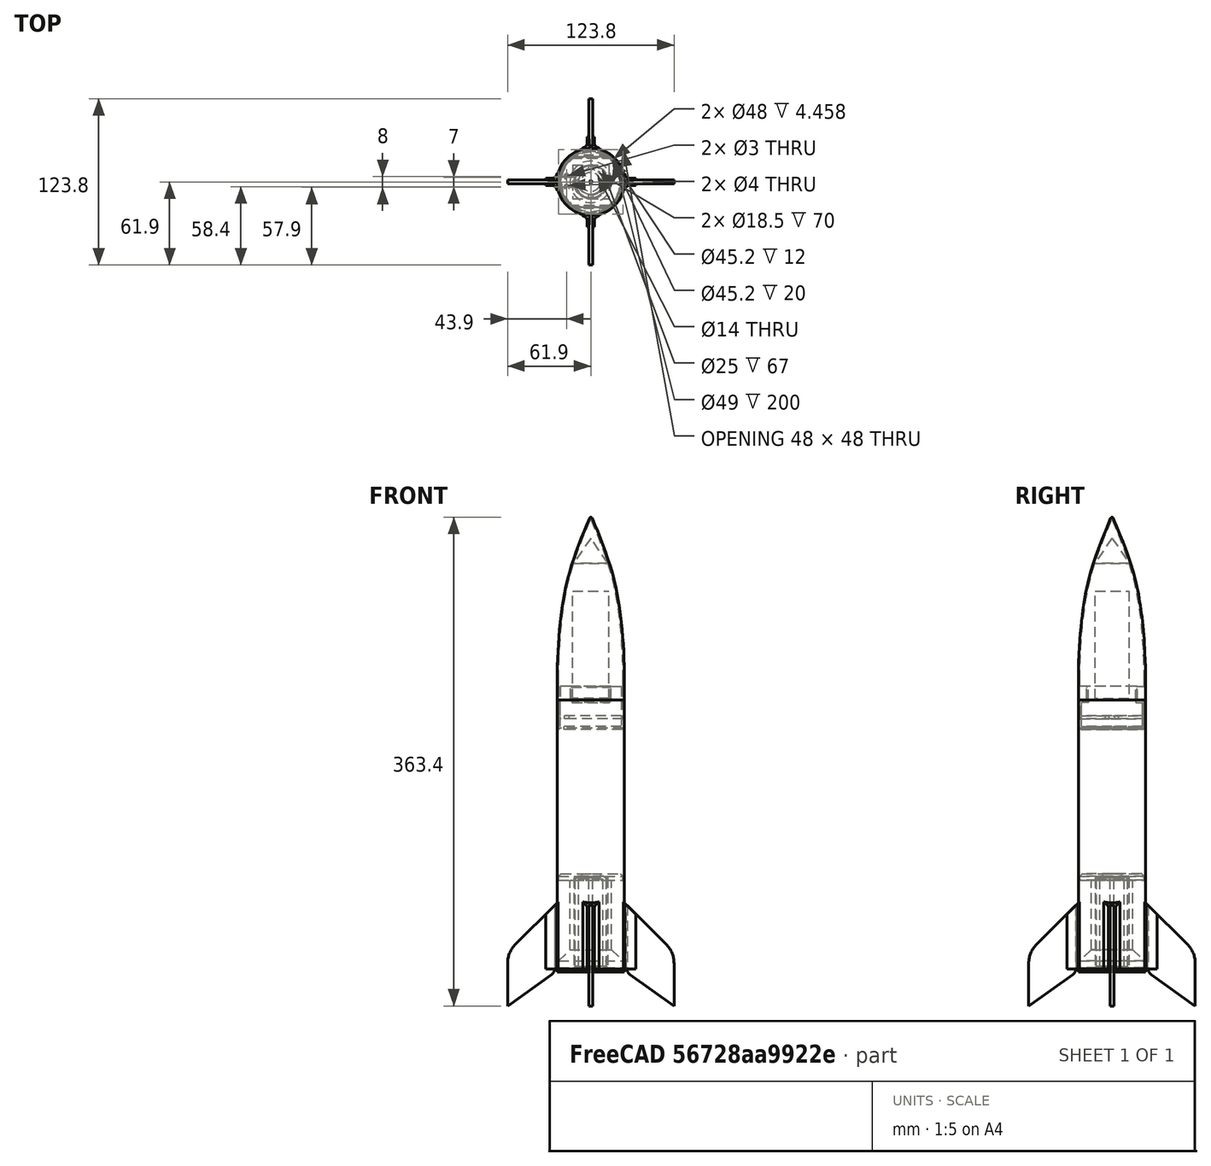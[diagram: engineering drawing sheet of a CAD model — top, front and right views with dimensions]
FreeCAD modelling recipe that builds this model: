
FCSTD DOCUMENT  (FreeCAD 0.19R)
Label: LaMule_V1
License: All rights reserved
LicenseURL: http://en.wikipedia.org/wiki/All_rights_reserved
objects: Sketcher::SketchObject×34, PartDesign::Pad×22, PartDesign::Body×17, PartDesign::Fillet×12, PartDesign::Chamfer×9, PartDesign::Pocket×8, Mesh::Feature×5, PartDesign::Revolution×4, App::LinkGroup×2, PartDesign::Thickness×2, TechDraw::DrawSVGTemplate×1, TechDraw::DrawViewPart×1, TechDraw::DrawPage×1
note: 165 computed .brp shape members not serialized (recipe doc carries the construction recipe); baked Part::Feature solids carry a one-line shape summary decoded from their .brp

FEATURE [Sketcher::SketchObject] Sketch
  FullyConstrained = true
  MapMode = 5
  Placement = pos=(0,0,0) rot=(1,0,0;1.5708rad)
  Support = -> [XZ_Plane]
  sketch-geometry (12):
    g0: LineSegment StartX=24 StartY=0 StartZ=0 EndX=7 EndY=0 EndZ=0
    g1: LineSegment StartX=7 StartY=0 StartZ=0 EndX=7 EndY=3 EndZ=0
    g2: LineSegment StartX=7 StartY=3 StartZ=0 EndX=12.5 EndY=3 EndZ=0
    g3: LineSegment StartX=12.5 StartY=3 StartZ=0 EndX=12.5 EndY=73 EndZ=0
    g4: LineSegment StartX=12.5 StartY=73 StartZ=0 EndX=25 EndY=73 EndZ=0
    g5: LineSegment StartX=25 StartY=73 StartZ=0 EndX=25 EndY=71 EndZ=0
    g6: LineSegment StartX=25 StartY=71 StartZ=0 EndX=24 EndY=70 EndZ=0
    g7: LineSegment StartX=24 StartY=70 StartZ=0 EndX=24 EndY=65 EndZ=0
    g8: LineSegment StartX=24 StartY=65 StartZ=0 EndX=15.5 EndY=56.5 EndZ=0
    g9: LineSegment StartX=15.5 StartY=56.5 StartZ=0 EndX=15.5 EndY=5 EndZ=0
    g10: LineSegment StartX=15.5 StartY=5 StartZ=0 EndX=24 EndY=5 EndZ=0
    g11: LineSegment StartX=24 StartY=5 StartZ=0 EndX=24 EndY=0 EndZ=0
  constraints (36):
    c: PointOnObject(g0,g-1)
    c: PointOnObject(g0,g-1)
    c: Coincident(g0,g1)
    c: Vertical(g1)
    c: Coincident(g1,g2)
    c: Horizontal(g2)
    c: Coincident(g2,g3)
    c: Vertical(g3)
    c: Coincident(g3,g4)
    c: Horizontal(g4)
    c: Coincident(g4,g5)
    c: Coincident(g5,g6)
    c: Coincident(g6,g7)
    c: Vertical(g7)
    c: Coincident(g7,g8)
    c: Coincident(g8,g9)
    c: Vertical(g9)
    c: Coincident(g9,g10)
    c: Horizontal(g10)
    c: Coincident(g10,g11)
    c: Coincident(g11,g0)
    c: DistanceX(g-2,g2) = 12.5
    c: DistanceY(g3,g3) = 70
    c: DistanceY(g1,g1) = 3
    c: DistanceX(g-2,g4) = 25
    c: Vertical(g5)
    c: DistanceY(g5,g5) = 2
    c: DistanceY(g7,g7) = 5
    c: DistanceX(g-1,g0) = 24
    c: DistanceX(g-2,g7) = 24
    c: Distance(g9,g3) = 3
    c: DistanceY(g11,g11) = 5
    c: Angle(g9,g8) = 2.35619
    c: Angle(g7,g6) = 2.35619
    c: Vertical(g11)
    c: DistanceX(g-2,g0) = 7
FEATURE [PartDesign::Revolution] Revolution
  Angle = 360
  Axis = (0,2e-16,1)
  Base = (0,0,0)
  Placement = pos=(0,0,0) rot=(1,0,0;1.5708rad)
  Profile = -> Sketch
  ReferenceAxis = -> Sketch [V_Axis]
  Reversed = true
FEATURE [PartDesign::Chamfer] Chamfer
  Angle = 45
  Base = -> Revolution [Edge6]
  BaseFeature = -> Revolution
  ChamferType = 0
  FlipDirection = false
  Placement = pos=(0,0,0) rot=(1,0,0;1.5708rad)
  Size = 3
  Size2 = 1
  SupportTransform = false
FEATURE [PartDesign::Chamfer] Chamfer001
  Angle = 45
  Base = -> Chamfer [Edge12]
  BaseFeature = -> Chamfer
  ChamferType = 0
  FlipDirection = false
  Placement = pos=(0,0,0) rot=(1,0,0;1.5708rad)
  Size = 2
  Size2 = 1
  SupportTransform = false
FEATURE [PartDesign::Body] Body  label="support_moteur_V1"
  Group = -> [Sketch,Revolution,Chamfer,Chamfer001]
  Origin = -> Origin
  Placement = pos=(7e-15,0,71) rot=(0,1,0;3.14159rad)
  Tip = -> Chamfer001
FEATURE [Sketcher::SketchObject] Sketch001
  FullyConstrained = true
  MapMode = 5
  Support = -> [XY_Plane001]
  sketch-geometry (2):
    g0: Circle CenterX=0 CenterY=0 CenterZ=0 NormalX=0 NormalY=0 NormalZ=1 AngleXU=0 Radius=24.5
    g1: Circle CenterX=0 CenterY=0 CenterZ=0 NormalX=0 NormalY=0 NormalZ=1 AngleXU=0 Radius=25
  constraints (4):
    c: Radius(g0) = 24.5
    c: Radius(g1) = 25
    c: Coincident(g0,g-1)
    c: Coincident(g1,g0)
FEATURE [PartDesign::Pad] Pad
  Direction = (1,1,1)
  Length = 200
  Length2 = 100
  Profile = -> Sketch001
  Type = 0
FEATURE [PartDesign::Body] Body001  label="tube_V1"
  Group = -> [Sketch001,Pad]
  Origin = -> Origin001
  Tip = -> Pad
FEATURE [Sketcher::SketchObject] Sketch002
  FullyConstrained = true
  MapMode = 5
  Support = -> [XY_Plane002]
  sketch-geometry (12):
    g0: ArcOfCircle CenterX=0 CenterY=0 CenterZ=0 NormalX=0 NormalY=0 NormalZ=1 AngleXU=0 Radius=25 StartAngle=6.04082 EndAngle=6.52555
    g1: LineSegment StartX=24.2693 StartY=-6 StartZ=0 EndX=25.2982 EndY=-6 EndZ=0
    g2: LineSegment StartX=24.2693 StartY=6 StartZ=0 EndX=25.2982 EndY=6 EndZ=0
    g3: LineSegment StartX=25.8697 StartY=2.6 StartZ=0 EndX=33.4517 EndY=2.6 EndZ=0
    g4: LineSegment StartX=33.4517 StartY=2.6 StartZ=0 EndX=33.4517 EndY=1.6 EndZ=0
    g5: LineSegment StartX=33.4517 StartY=1.6 StartZ=0 EndX=26.4517 EndY=1.6 EndZ=0
    g6: LineSegment StartX=26.4517 StartY=1.6 StartZ=0 EndX=26.4517 EndY=-1.6 EndZ=0
    g7: LineSegment StartX=26.4517 StartY=-1.6 StartZ=0 EndX=33.4517 EndY=-1.6 EndZ=0
    g8: LineSegment StartX=33.4517 StartY=-1.6 StartZ=0 EndX=33.4517 EndY=-2.6 EndZ=0
    g9: LineSegment StartX=33.4517 StartY=-2.6 StartZ=0 EndX=25.8697 EndY=-2.6 EndZ=0
    g10: ArcOfCircle CenterX=0 CenterY=0 CenterZ=0 NormalX=0 NormalY=0 NormalZ=1 AngleXU=0 Radius=26 StartAngle=6.05032 EndAngle=6.18302
    g11: ArcOfCircle CenterX=0 CenterY=0 CenterZ=0 NormalX=0 NormalY=0 NormalZ=1 AngleXU=0 Radius=26 StartAngle=0.100167 EndAngle=0.232868
  constraints (33):
    c: Coincident(g0,g-1)
    c: Radius(g0) = 25
    c: Coincident(g0,g1)
    c: Coincident(g0,g2)
    c: Horizontal(g3)
    c: Coincident(g3,g4)
    c: Coincident(g4,g5)
    c: Horizontal(g5)
    c: Coincident(g5,g6)
    c: Coincident(g6,g7)
    c: Horizontal(g7)
    c: Coincident(g7,g8)
    c: Coincident(g8,g9)
    c: Horizontal(g9)
    c: Coincident(g10,g0)
    c: Coincident(g10,g1)
    c: Coincident(g10,g9)
    c: Coincident(g11,g0)
    c: Coincident(g11,g2)
    c: Coincident(g11,g3)
    c: Radius(g11) = 26
    c: Horizontal(g2)
    c: Horizontal(g1)
    c: Symmetric(g7,g4,g-1)
    c: Vertical(g8)
    c: Vertical(g6)
    c: Distance(g6,g5) = 3.2
    c: DistanceY(g4,g4) = 1
    c: Distance(g5,g0) = 26.5
    c: Symmetric(g3,g8,g-1)
    c: DistanceX(g5,g5) = 7
    c: Symmetric(g2,g1,g-1)
    c: DistanceY(g-1,g2) = 6
FEATURE [PartDesign::Pad] Pad001
  Direction = (1,1,1)
  Length = 50
  Length2 = 100
  Profile = -> Sketch002
  Type = 0
FEATURE [PartDesign::Fillet] Fillet
  Base = -> Pad001 [Edge20,Edge1]
  BaseFeature = -> Pad001
  Radius = 4
  SupportTransform = false
FEATURE [Sketcher::SketchObject] Sketch003
  ExternalGeometry = -> [Fillet]
  FullyConstrained = true
  MapMode = 5
  Placement = pos=(0,-2.6,0) rot=(1,0,0;1.5708rad)
  Support = -> [Fillet]
  sketch-geometry (3):
    g0: LineSegment StartX=33.4517 StartY=50 StartZ=0 EndX=33.4517 EndY=40.8177 EndZ=0
    g1: LineSegment StartX=33.4517 StartY=40.8177 StartZ=0 EndX=24.2693 EndY=50 EndZ=0
    g2: LineSegment StartX=24.2693 StartY=50 StartZ=0 EndX=33.4517 EndY=50 EndZ=0
  constraints (8):
    c: Coincident(g-4,g0)
    c: PointOnObject(g0,g-4)
    c: Coincident(g0,g1)
    c: PointOnObject(g1,g-3)
    c: Coincident(g1,g2)
    c: Coincident(g2,g0)
    c: Horizontal(g2)
    c: Angle(g1,g2) = 0.785398
FEATURE [PartDesign::Pocket] Pocket
  BaseFeature = -> Fillet
  Length = 23
  Length2 = 100
  Midplane = true
  Profile = -> Sketch003
  Type = 1
FEATURE [PartDesign::Body] Body002  label="support_aileron_V1"
  Group = -> [Sketch002,Pad001,Fillet,Sketch003,Pocket]
  Origin = -> Origin002
  Tip = -> Pocket
FEATURE [Sketcher::SketchObject] Sketch004
  FullyConstrained = true
  MapMode = 5
  Support = -> [XY_Plane003]
  sketch-geometry (12):
    g0: ArcOfCircle CenterX=0 CenterY=0 CenterZ=0 NormalX=0 NormalY=0 NormalZ=1 AngleXU=0 Radius=25 StartAngle=6.04082 EndAngle=6.52555
    g1: LineSegment StartX=24.2693 StartY=-6 StartZ=0 EndX=25.2982 EndY=-6 EndZ=0
    g2: LineSegment StartX=24.2693 StartY=6 StartZ=0 EndX=25.2982 EndY=6 EndZ=0
    g3: LineSegment StartX=25.8697 StartY=2.6 StartZ=0 EndX=33.4517 EndY=2.6 EndZ=0
    g4: LineSegment StartX=33.4517 StartY=2.6 StartZ=0 EndX=33.4517 EndY=1.6 EndZ=0
    g5: LineSegment StartX=33.4517 StartY=1.6 StartZ=0 EndX=26.4517 EndY=1.6 EndZ=0
    g6: LineSegment StartX=26.4517 StartY=1.6 StartZ=0 EndX=26.4517 EndY=-1.6 EndZ=0
    g7: LineSegment StartX=26.4517 StartY=-1.6 StartZ=0 EndX=33.4517 EndY=-1.6 EndZ=0
    g8: LineSegment StartX=33.4517 StartY=-1.6 StartZ=0 EndX=33.4517 EndY=-2.6 EndZ=0
    g9: LineSegment StartX=33.4517 StartY=-2.6 StartZ=0 EndX=25.8697 EndY=-2.6 EndZ=0
    g10: ArcOfCircle CenterX=0 CenterY=0 CenterZ=0 NormalX=0 NormalY=0 NormalZ=1 AngleXU=0 Radius=26 StartAngle=6.05032 EndAngle=6.18302
    g11: ArcOfCircle CenterX=0 CenterY=0 CenterZ=0 NormalX=0 NormalY=0 NormalZ=1 AngleXU=0 Radius=26 StartAngle=0.100167 EndAngle=0.232868
  constraints (33):
    c: Coincident(g0,g-1)
    c: Radius(g0) = 25
    c: Coincident(g0,g1)
    c: Coincident(g0,g2)
    c: Horizontal(g3)
    c: Coincident(g3,g4)
    c: Coincident(g4,g5)
    c: Horizontal(g5)
    c: Coincident(g5,g6)
    c: Coincident(g6,g7)
    c: Horizontal(g7)
    c: Coincident(g7,g8)
    c: Coincident(g8,g9)
    c: Horizontal(g9)
    c: Coincident(g10,g0)
    c: Coincident(g10,g1)
    c: Coincident(g10,g9)
    c: Coincident(g11,g0)
    c: Coincident(g11,g2)
    c: Coincident(g11,g3)
    c: Radius(g11) = 26
    c: Horizontal(g2)
    c: Horizontal(g1)
    c: Symmetric(g7,g4,g-1)
    c: Vertical(g8)
    c: Vertical(g6)
    c: Distance(g6,g5) = 3.2
    c: DistanceY(g4,g4) = 1
    c: Distance(g5,g0) = 26.5
    c: Symmetric(g3,g8,g-1)
    c: DistanceX(g5,g5) = 7
    c: Symmetric(g2,g1,g-1)
    c: DistanceY(g-1,g2) = 6
FEATURE [PartDesign::Pad] Pad002
  Direction = (1,1,1)
  Length = 50
  Length2 = 100
  Profile = -> Sketch004
  Type = 0
FEATURE [PartDesign::Fillet] Fillet001
  Base = -> Pad002 [Edge20,Edge1]
  BaseFeature = -> Pad002
  Radius = 4
  SupportTransform = false
FEATURE [Sketcher::SketchObject] Sketch005
  ExternalGeometry = -> [Fillet001]
  FullyConstrained = true
  MapMode = 5
  Placement = pos=(0,-2.6,0) rot=(1,0,0;1.5708rad)
  Support = -> [Fillet001]
  sketch-geometry (3):
    g0: LineSegment StartX=33.4517 StartY=50 StartZ=0 EndX=33.4517 EndY=40.8177 EndZ=0
    g1: LineSegment StartX=33.4517 StartY=40.8177 StartZ=0 EndX=24.2693 EndY=50 EndZ=0
    g2: LineSegment StartX=24.2693 StartY=50 StartZ=0 EndX=33.4517 EndY=50 EndZ=0
  constraints (8):
    c: Coincident(g-4,g0)
    c: PointOnObject(g0,g-4)
    c: Coincident(g0,g1)
    c: PointOnObject(g1,g-3)
    c: Coincident(g1,g2)
    c: Coincident(g2,g0)
    c: Horizontal(g2)
    c: Angle(g1,g2) = 0.785398
FEATURE [PartDesign::Pocket] Pocket001
  BaseFeature = -> Fillet001
  Length = 23
  Length2 = 100
  Midplane = true
  Profile = -> Sketch005
  Type = 1
FEATURE [PartDesign::Body] Body003  label="support_aileron_V002"
  Group = -> [Sketch004,Pad002,Fillet001,Sketch005,Pocket001]
  Origin = -> Origin003
  Placement = pos=(0,0,0) rot=(0,0,1;1.5708rad)
  Tip = -> Pocket001
FEATURE [Sketcher::SketchObject] Sketch006
  FullyConstrained = true
  MapMode = 5
  Support = -> [XY_Plane004]
  sketch-geometry (12):
    g0: ArcOfCircle CenterX=0 CenterY=0 CenterZ=0 NormalX=0 NormalY=0 NormalZ=1 AngleXU=0 Radius=25 StartAngle=6.04082 EndAngle=6.52555
    g1: LineSegment StartX=24.2693 StartY=-6 StartZ=0 EndX=25.2982 EndY=-6 EndZ=0
    g2: LineSegment StartX=24.2693 StartY=6 StartZ=0 EndX=25.2982 EndY=6 EndZ=0
    g3: LineSegment StartX=25.8697 StartY=2.6 StartZ=0 EndX=33.4517 EndY=2.6 EndZ=0
    g4: LineSegment StartX=33.4517 StartY=2.6 StartZ=0 EndX=33.4517 EndY=1.6 EndZ=0
    g5: LineSegment StartX=33.4517 StartY=1.6 StartZ=0 EndX=26.4517 EndY=1.6 EndZ=0
    g6: LineSegment StartX=26.4517 StartY=1.6 StartZ=0 EndX=26.4517 EndY=-1.6 EndZ=0
    g7: LineSegment StartX=26.4517 StartY=-1.6 StartZ=0 EndX=33.4517 EndY=-1.6 EndZ=0
    g8: LineSegment StartX=33.4517 StartY=-1.6 StartZ=0 EndX=33.4517 EndY=-2.6 EndZ=0
    g9: LineSegment StartX=33.4517 StartY=-2.6 StartZ=0 EndX=25.8697 EndY=-2.6 EndZ=0
    g10: ArcOfCircle CenterX=0 CenterY=0 CenterZ=0 NormalX=0 NormalY=0 NormalZ=1 AngleXU=0 Radius=26 StartAngle=6.05032 EndAngle=6.18302
    g11: ArcOfCircle CenterX=0 CenterY=0 CenterZ=0 NormalX=0 NormalY=0 NormalZ=1 AngleXU=0 Radius=26 StartAngle=0.100167 EndAngle=0.232868
  constraints (33):
    c: Coincident(g0,g-1)
    c: Radius(g0) = 25
    c: Coincident(g0,g1)
    c: Coincident(g0,g2)
    c: Horizontal(g3)
    c: Coincident(g3,g4)
    c: Coincident(g4,g5)
    c: Horizontal(g5)
    c: Coincident(g5,g6)
    c: Coincident(g6,g7)
    c: Horizontal(g7)
    c: Coincident(g7,g8)
    c: Coincident(g8,g9)
    c: Horizontal(g9)
    c: Coincident(g10,g0)
    c: Coincident(g10,g1)
    c: Coincident(g10,g9)
    c: Coincident(g11,g0)
    c: Coincident(g11,g2)
    c: Coincident(g11,g3)
    c: Radius(g11) = 26
    c: Horizontal(g2)
    c: Horizontal(g1)
    c: Symmetric(g7,g4,g-1)
    c: Vertical(g8)
    c: Vertical(g6)
    c: Distance(g6,g5) = 3.2
    c: DistanceY(g4,g4) = 1
    c: Distance(g5,g0) = 26.5
    c: Symmetric(g3,g8,g-1)
    c: DistanceX(g5,g5) = 7
    c: Symmetric(g2,g1,g-1)
    c: DistanceY(g-1,g2) = 6
FEATURE [PartDesign::Pad] Pad003
  Direction = (1,1,1)
  Length = 50
  Length2 = 100
  Profile = -> Sketch006
  Type = 0
FEATURE [PartDesign::Fillet] Fillet002
  Base = -> Pad003 [Edge20,Edge1]
  BaseFeature = -> Pad003
  Radius = 4
  SupportTransform = false
FEATURE [Sketcher::SketchObject] Sketch007
  ExternalGeometry = -> [Fillet002]
  FullyConstrained = true
  MapMode = 5
  Placement = pos=(0,-2.6,0) rot=(1,0,0;1.5708rad)
  Support = -> [Fillet002]
  sketch-geometry (3):
    g0: LineSegment StartX=33.4517 StartY=50 StartZ=0 EndX=33.4517 EndY=40.8177 EndZ=0
    g1: LineSegment StartX=33.4517 StartY=40.8177 StartZ=0 EndX=24.2693 EndY=50 EndZ=0
    g2: LineSegment StartX=24.2693 StartY=50 StartZ=0 EndX=33.4517 EndY=50 EndZ=0
  constraints (8):
    c: Coincident(g-4,g0)
    c: PointOnObject(g0,g-4)
    c: Coincident(g0,g1)
    c: PointOnObject(g1,g-3)
    c: Coincident(g1,g2)
    c: Coincident(g2,g0)
    c: Horizontal(g2)
    c: Angle(g1,g2) = 0.785398
FEATURE [PartDesign::Pocket] Pocket002
  BaseFeature = -> Fillet002
  Length = 23
  Length2 = 100
  Midplane = true
  Profile = -> Sketch007
  Type = 1
FEATURE [PartDesign::Body] Body004  label="support_aileron_V003"
  Group = -> [Sketch006,Pad003,Fillet002,Sketch007,Pocket002]
  Origin = -> Origin004
  Placement = pos=(0,0,0) rot=(0,0,1;3.14159rad)
  Tip = -> Pocket002
FEATURE [Sketcher::SketchObject] Sketch008
  FullyConstrained = true
  MapMode = 5
  Support = -> [XY_Plane005]
  sketch-geometry (12):
    g0: ArcOfCircle CenterX=0 CenterY=0 CenterZ=0 NormalX=0 NormalY=0 NormalZ=1 AngleXU=0 Radius=25 StartAngle=6.04082 EndAngle=6.52555
    g1: LineSegment StartX=24.2693 StartY=-6 StartZ=0 EndX=25.2982 EndY=-6 EndZ=0
    g2: LineSegment StartX=24.2693 StartY=6 StartZ=0 EndX=25.2982 EndY=6 EndZ=0
    g3: LineSegment StartX=25.8697 StartY=2.6 StartZ=0 EndX=33.4517 EndY=2.6 EndZ=0
    g4: LineSegment StartX=33.4517 StartY=2.6 StartZ=0 EndX=33.4517 EndY=1.6 EndZ=0
    g5: LineSegment StartX=33.4517 StartY=1.6 StartZ=0 EndX=26.4517 EndY=1.6 EndZ=0
    g6: LineSegment StartX=26.4517 StartY=1.6 StartZ=0 EndX=26.4517 EndY=-1.6 EndZ=0
    g7: LineSegment StartX=26.4517 StartY=-1.6 StartZ=0 EndX=33.4517 EndY=-1.6 EndZ=0
    g8: LineSegment StartX=33.4517 StartY=-1.6 StartZ=0 EndX=33.4517 EndY=-2.6 EndZ=0
    g9: LineSegment StartX=33.4517 StartY=-2.6 StartZ=0 EndX=25.8697 EndY=-2.6 EndZ=0
    g10: ArcOfCircle CenterX=0 CenterY=0 CenterZ=0 NormalX=0 NormalY=0 NormalZ=1 AngleXU=0 Radius=26 StartAngle=6.05032 EndAngle=6.18302
    g11: ArcOfCircle CenterX=0 CenterY=0 CenterZ=0 NormalX=0 NormalY=0 NormalZ=1 AngleXU=0 Radius=26 StartAngle=0.100167 EndAngle=0.232868
  constraints (33):
    c: Coincident(g0,g-1)
    c: Radius(g0) = 25
    c: Coincident(g0,g1)
    c: Coincident(g0,g2)
    c: Horizontal(g3)
    c: Coincident(g3,g4)
    c: Coincident(g4,g5)
    c: Horizontal(g5)
    c: Coincident(g5,g6)
    c: Coincident(g6,g7)
    c: Horizontal(g7)
    c: Coincident(g7,g8)
    c: Coincident(g8,g9)
    c: Horizontal(g9)
    c: Coincident(g10,g0)
    c: Coincident(g10,g1)
    c: Coincident(g10,g9)
    c: Coincident(g11,g0)
    c: Coincident(g11,g2)
    c: Coincident(g11,g3)
    c: Radius(g11) = 26
    c: Horizontal(g2)
    c: Horizontal(g1)
    c: Symmetric(g7,g4,g-1)
    c: Vertical(g8)
    c: Vertical(g6)
    c: Distance(g6,g5) = 3.2
    c: DistanceY(g4,g4) = 1
    c: Distance(g5,g0) = 26.5
    c: Symmetric(g3,g8,g-1)
    c: DistanceX(g5,g5) = 7
    c: Symmetric(g2,g1,g-1)
    c: DistanceY(g-1,g2) = 6
FEATURE [PartDesign::Pad] Pad004
  Direction = (1,1,1)
  Length = 50
  Length2 = 100
  Profile = -> Sketch008
  Type = 0
FEATURE [PartDesign::Fillet] Fillet003
  Base = -> Pad004 [Edge20,Edge1]
  BaseFeature = -> Pad004
  Radius = 4
  SupportTransform = false
FEATURE [Sketcher::SketchObject] Sketch009
  ExternalGeometry = -> [Fillet003]
  FullyConstrained = true
  MapMode = 5
  Placement = pos=(0,-2.6,0) rot=(1,0,0;1.5708rad)
  Support = -> [Fillet003]
  sketch-geometry (3):
    g0: LineSegment StartX=33.4517 StartY=50 StartZ=0 EndX=33.4517 EndY=40.8177 EndZ=0
    g1: LineSegment StartX=33.4517 StartY=40.8177 StartZ=0 EndX=24.2693 EndY=50 EndZ=0
    g2: LineSegment StartX=24.2693 StartY=50 StartZ=0 EndX=33.4517 EndY=50 EndZ=0
  constraints (8):
    c: Coincident(g-4,g0)
    c: PointOnObject(g0,g-4)
    c: Coincident(g0,g1)
    c: PointOnObject(g1,g-3)
    c: Coincident(g1,g2)
    c: Coincident(g2,g0)
    c: Horizontal(g2)
    c: Angle(g1,g2) = 0.785398
FEATURE [PartDesign::Pocket] Pocket003
  BaseFeature = -> Fillet003
  Length = 23
  Length2 = 100
  Midplane = true
  Profile = -> Sketch009
  Type = 1
FEATURE [PartDesign::Body] Body005  label="support_aileron_V004"
  Group = -> [Sketch008,Pad004,Fillet003,Sketch009,Pocket003]
  Origin = -> Origin005
  Placement = pos=(0,0,0) rot=(0,0,-1;1.5708rad)
  Tip = -> Pocket003
FEATURE [App::LinkGroup] LinkGroup  label="support_ailerons_V1"
  ElementList = -> [Body005,Body004,Body003,Body002]
  LinkMode = 0
FEATURE [Sketcher::SketchObject] Sketch010
  FullyConstrained = true
  MapMode = 5
  Placement = pos=(0,0,0) rot=(0.57735,0.57735,0.57735;2.0944rad)
  Support = -> [YZ_Plane006]
  sketch-geometry (4):
    g0: LineSegment StartX=27 StartY=-2.5 StartZ=0 EndX=61.9 EndY=-27.4 EndZ=0
    g1: LineSegment StartX=61.9 StartY=-27.4 StartZ=0 EndX=61.9 EndY=12.6 EndZ=0
    g2: LineSegment StartX=61.9 StartY=12.6 StartZ=0 EndX=27 EndY=47.5 EndZ=0
    g3: LineSegment StartX=27 StartY=47.5 StartZ=0 EndX=27 EndY=-2.5 EndZ=0
  constraints (12):
    c: Coincident(g0,g1)
    c: Vertical(g1)
    c: Coincident(g1,g2)
    c: Coincident(g2,g3)
    c: Coincident(g3,g0)
    c: Vertical(g3)
    c: DistanceY(g3,g3) = 50
    c: DistanceY(g-1,g2) = 47.5
    c: DistanceX(g-2,g0) = 27
    c: Angle(g3,g2) = 0.785398
    c: DistanceY(g1,g1) = 40
    c: DistanceX(g-2,g0) = 61.9
FEATURE [PartDesign::Pad] Pad005
  Direction = (1,1,1)
  Length = 3
  Length2 = 100
  Midplane = true
  Placement = pos=(0,0,0) rot=(0.57735,0.57735,0.57735;2.0944rad)
  Profile = -> Sketch010
  Type = 0
FEATURE [PartDesign::Fillet] Fillet004
  Base = -> Pad005 [Edge5]
  BaseFeature = -> Pad005
  Placement = pos=(0,0,0) rot=(0.57735,0.57735,0.57735;2.0944rad)
  Radius = 20
  SupportTransform = false
FEATURE [PartDesign::Fillet] Fillet005
  Base = -> Fillet004 [Edge11]
  BaseFeature = -> Fillet004
  Placement = pos=(0,0,0) rot=(0.57735,0.57735,0.57735;2.0944rad)
  Radius = 5
  SupportTransform = false
FEATURE [PartDesign::Body] Body006  label="ailerons_V1"
  Group = -> [Sketch010,Pad005,Fillet004,Fillet005]
  Origin = -> Origin006
  Tip = -> Fillet005
FEATURE [Sketcher::SketchObject] Sketch011
  FullyConstrained = true
  MapMode = 5
  Placement = pos=(0,0,0) rot=(0.57735,0.57735,0.57735;2.0944rad)
  Support = -> [YZ_Plane007]
  sketch-geometry (4):
    g0: LineSegment StartX=27 StartY=-2.5 StartZ=0 EndX=61.9 EndY=-27.4 EndZ=0
    g1: LineSegment StartX=61.9 StartY=-27.4 StartZ=0 EndX=61.9 EndY=12.6 EndZ=0
    g2: LineSegment StartX=61.9 StartY=12.6 StartZ=0 EndX=27 EndY=47.5 EndZ=0
    g3: LineSegment StartX=27 StartY=47.5 StartZ=0 EndX=27 EndY=-2.5 EndZ=0
  constraints (12):
    c: Coincident(g0,g1)
    c: Vertical(g1)
    c: Coincident(g1,g2)
    c: Coincident(g2,g3)
    c: Coincident(g3,g0)
    c: Vertical(g3)
    c: DistanceY(g3,g3) = 50
    c: DistanceY(g-1,g2) = 47.5
    c: DistanceX(g-2,g0) = 27
    c: Angle(g3,g2) = 0.785398
    c: DistanceY(g1,g1) = 40
    c: DistanceX(g-2,g0) = 61.9
FEATURE [PartDesign::Pad] Pad006
  Direction = (1,1,1)
  Length = 3
  Length2 = 100
  Midplane = true
  Placement = pos=(0,0,0) rot=(0.57735,0.57735,0.57735;2.0944rad)
  Profile = -> Sketch011
  Type = 0
FEATURE [PartDesign::Fillet] Fillet006
  Base = -> Pad006 [Edge5]
  BaseFeature = -> Pad006
  Placement = pos=(0,0,0) rot=(0.57735,0.57735,0.57735;2.0944rad)
  Radius = 20
  SupportTransform = false
FEATURE [PartDesign::Fillet] Fillet007
  Base = -> Fillet006 [Edge11]
  BaseFeature = -> Fillet006
  Placement = pos=(0,0,0) rot=(0.57735,0.57735,0.57735;2.0944rad)
  Radius = 5
  SupportTransform = false
FEATURE [PartDesign::Body] Body007  label="ailerons_V002"
  Group = -> [Sketch011,Pad006,Fillet006,Fillet007]
  Origin = -> Origin007
  Placement = pos=(0,0,0) rot=(0,0,1;3.14159rad)
  Tip = -> Fillet007
FEATURE [Sketcher::SketchObject] Sketch012
  FullyConstrained = true
  MapMode = 5
  Placement = pos=(0,0,0) rot=(0.57735,0.57735,0.57735;2.0944rad)
  Support = -> [YZ_Plane008]
  sketch-geometry (4):
    g0: LineSegment StartX=27 StartY=-2.5 StartZ=0 EndX=61.9 EndY=-27.4 EndZ=0
    g1: LineSegment StartX=61.9 StartY=-27.4 StartZ=0 EndX=61.9 EndY=12.6 EndZ=0
    g2: LineSegment StartX=61.9 StartY=12.6 StartZ=0 EndX=27 EndY=47.5 EndZ=0
    g3: LineSegment StartX=27 StartY=47.5 StartZ=0 EndX=27 EndY=-2.5 EndZ=0
  constraints (12):
    c: Coincident(g0,g1)
    c: Vertical(g1)
    c: Coincident(g1,g2)
    c: Coincident(g2,g3)
    c: Coincident(g3,g0)
    c: Vertical(g3)
    c: DistanceY(g3,g3) = 50
    c: DistanceY(g-1,g2) = 47.5
    c: DistanceX(g-2,g0) = 27
    c: Angle(g3,g2) = 0.785398
    c: DistanceY(g1,g1) = 40
    c: DistanceX(g-2,g0) = 61.9
FEATURE [PartDesign::Pad] Pad007
  Direction = (1,1,1)
  Length = 3
  Length2 = 100
  Midplane = true
  Placement = pos=(0,0,0) rot=(0.57735,0.57735,0.57735;2.0944rad)
  Profile = -> Sketch012
  Type = 0
FEATURE [PartDesign::Fillet] Fillet008
  Base = -> Pad007 [Edge5]
  BaseFeature = -> Pad007
  Placement = pos=(0,0,0) rot=(0.57735,0.57735,0.57735;2.0944rad)
  Radius = 20
  SupportTransform = false
FEATURE [PartDesign::Fillet] Fillet009
  Base = -> Fillet008 [Edge11]
  BaseFeature = -> Fillet008
  Placement = pos=(0,0,0) rot=(0.57735,0.57735,0.57735;2.0944rad)
  Radius = 5
  SupportTransform = false
FEATURE [PartDesign::Body] Body008  label="ailerons_V003"
  Group = -> [Sketch012,Pad007,Fillet008,Fillet009]
  Origin = -> Origin008
  Placement = pos=(0,0,0) rot=(0,0,1;1.5708rad)
  Tip = -> Fillet009
FEATURE [Sketcher::SketchObject] Sketch013
  FullyConstrained = true
  MapMode = 5
  Placement = pos=(0,0,0) rot=(0.57735,0.57735,0.57735;2.0944rad)
  Support = -> [YZ_Plane009]
  sketch-geometry (4):
    g0: LineSegment StartX=27 StartY=-2.5 StartZ=0 EndX=61.9 EndY=-27.4 EndZ=0
    g1: LineSegment StartX=61.9 StartY=-27.4 StartZ=0 EndX=61.9 EndY=12.6 EndZ=0
    g2: LineSegment StartX=61.9 StartY=12.6 StartZ=0 EndX=27 EndY=47.5 EndZ=0
    g3: LineSegment StartX=27 StartY=47.5 StartZ=0 EndX=27 EndY=-2.5 EndZ=0
  constraints (12):
    c: Coincident(g0,g1)
    c: Vertical(g1)
    c: Coincident(g1,g2)
    c: Coincident(g2,g3)
    c: Coincident(g3,g0)
    c: Vertical(g3)
    c: DistanceY(g3,g3) = 50
    c: DistanceY(g-1,g2) = 47.5
    c: DistanceX(g-2,g0) = 27
    c: Angle(g3,g2) = 0.785398
    c: DistanceY(g1,g1) = 40
    c: DistanceX(g-2,g0) = 61.9
FEATURE [PartDesign::Pad] Pad008
  Direction = (1,1,1)
  Length = 3
  Length2 = 100
  Midplane = true
  Placement = pos=(0,0,0) rot=(0.57735,0.57735,0.57735;2.0944rad)
  Profile = -> Sketch013
  Type = 0
FEATURE [PartDesign::Fillet] Fillet010
  Base = -> Pad008 [Edge5]
  BaseFeature = -> Pad008
  Placement = pos=(0,0,0) rot=(0.57735,0.57735,0.57735;2.0944rad)
  Radius = 20
  SupportTransform = false
FEATURE [PartDesign::Fillet] Fillet011
  Base = -> Fillet010 [Edge11]
  BaseFeature = -> Fillet010
  Placement = pos=(0,0,0) rot=(0.57735,0.57735,0.57735;2.0944rad)
  Radius = 5
  SupportTransform = false
FEATURE [PartDesign::Body] Body009  label="ailerons_V004"
  Group = -> [Sketch013,Pad008,Fillet010,Fillet011]
  Origin = -> Origin009
  Placement = pos=(0,0,0) rot=(0,0,-1;1.5708rad)
  Tip = -> Fillet011
FEATURE [App::LinkGroup] LinkGroup001  label="ailerons"
  ElementList = -> [Body009,Body008,Body007,Body006]
  LinkMode = 0
FEATURE [Sketcher::SketchObject] Sketch014
  FullyConstrained = true
  MapMode = 5
  Support = -> [XY_Plane010]
  sketch-geometry (12):
    g0: LineSegment StartX=0 StartY=0 StartZ=0 EndX=134.73 EndY=0 EndZ=0
    g1: LineSegment StartX=134.73 StartY=-24 StartZ=0 EndX=134.73 EndY=0 EndZ=0
    g2: LineSegment StartX=134.73 StartY=-24 StartZ=0 EndX=120.272 EndY=-24 EndZ=0
    g3-g7: Circle x5 (B-spline internal-alignment scaffolding for g8; pole/knot coordinates omitted)
    g8: BSplineCurve PolesCount=5 KnotsCount=3 Degree=3 IsPeriodic=0
    g9: GeomPoint X=120.272 Y=-24 Z=0
    g10: GeomPoint X=62.1183 Y=-19.6849 Z=0
    g11: GeomPoint X=0 Y=0 Z=0
  constraints (23):
    c: Coincident(g0,g-1)
    c: PointOnObject(g0,g-1)
    c: Coincident(g1,g0)
    c: Vertical(g1)
    c: Coincident(g2,g1)
    c: Horizontal(g2)
    c: Coincident(g8,g2)
    c: Weight(g3) = 1
    c: Equal(g3, g4-g7) x4
    c: Coincident(g8,g0)
    c: InternalAlignment(g3-g7 -> g8) x5
    c: InternalAlignment(g9,g8)
    c: InternalAlignment(g10,g8)
    c: InternalAlignment(g11,g8)
    c: DistanceX(g6) = 33.4091
    c: DistanceY(g6) = -14.1378
    c: DistanceX(g5) = 61.0359
    c: DistanceY(g5) = -20.426
    c: DistanceX(g4) = 92.9923
    c: DistanceY(g4) = -23.75
    c: DistanceX(g2) = 120.272
    c: DistanceY(g2) = -24
    c: DistanceX(g0,g0) = 134.73
FEATURE [PartDesign::Revolution] Revolution001
  Angle = 360
  Axis = (1,0,0)
  Base = (0,0,0)
  Profile = -> Sketch014
  ReferenceAxis = -> X_Axis010
  Reversed = true
FEATURE [PartDesign::Thickness] Thickness
  Base = -> Revolution001 [Face1]
  BaseFeature = -> Revolution001
  Intersection = false
  Join = 0
  Mode = 0
  SupportTransform = false
  Value = 1
FEATURE [Sketcher::SketchObject] Sketch015
  FullyConstrained = true
  MapMode = 5
  Placement = pos=(134.73,0,0) rot=(0.57735,0.57735,0.57735;2.0944rad)
  Support = -> [Thickness]
  sketch-geometry (5):
    g0: Circle CenterX=1.1e-15 CenterY=0 CenterZ=0 NormalX=0 NormalY=0 NormalZ=1 AngleXU=0 Radius=25
    g1: ArcOfCircle CenterX=1.1e-15 CenterY=0 CenterZ=0 NormalX=0 NormalY=0 NormalZ=1 AngleXU=0 Radius=24 StartAngle=0.675132 EndAngle=2.46646
    g2: ArcOfCircle CenterX=1.1e-15 CenterY=0 CenterZ=0 NormalX=0 NormalY=0 NormalZ=1 AngleXU=0 Radius=24 StartAngle=3.81672 EndAngle=5.60805
    g3: LineSegment StartX=-18.735 StartY=15 StartZ=0 EndX=-18.735 EndY=-15 EndZ=0
    g4: LineSegment StartX=18.735 StartY=15 StartZ=0 EndX=18.735 EndY=-15 EndZ=0
  constraints (14):
    c: Coincident(g0,g-1)
    c: Radius(g0) = 25
    c: Coincident(g1,g0)
    c: Coincident(g2,g0)
    c: Symmetric(g2,g2,g-2)
    c: Symmetric(g2,g1,g-1)
    c: Radius(g1) = 24
    c: Equal(g1,g2)
    c: Coincident(g3,g1)
    c: Coincident(g3,g2)
    c: Coincident(g4,g1)
    c: Coincident(g4,g2)
    c: Symmetric(g1,g1,g-2)
    c: DistanceY(g4,g4) = 30
FEATURE [PartDesign::Pad] Pad009
  BaseFeature = -> Thickness
  Direction = (1,1,1)
  Length = 10
  Length2 = 100
  Profile = -> Sketch015
  Reversed = true
  Type = 0
FEATURE [PartDesign::Chamfer] Chamfer002
  Angle = 45
  Base = -> Pad009 [Edge9,Edge6]
  BaseFeature = -> Pad009
  ChamferType = 0
  FlipDirection = false
  Size = 1
  Size2 = 1
  SupportTransform = false
FEATURE [PartDesign::Body] Body010  label="coiffe_V1"
  Group = -> [Sketch014,Revolution001,Thickness,Sketch015,Pad009,Chamfer002]
  Origin = -> Origin010
  Placement = pos=(-7.4e-14,0,335) rot=(0,1,0;1.5708rad)
  Tip = -> Chamfer002
FEATURE [Mesh::Feature] Mesh  label="coiffe_V1 (Meshed)"
FEATURE [TechDraw::DrawSVGTemplate] Template
  EditableTexts = Approved1=N/A; Approved2=N/A; CheckedBy=Papas Inventeurs; Code=Code; CompanyAddress=planête Terre, système solaire; CompanyName=Lift Off; DrawingNumber=1; DrawingTitle1=LaMule; DrawingTitle2=Envoyons quelque chose en l'air!; DrawingTitle3="Just because"; DrawnBy=Maël & PéPé; Revision=Rev 1; Scale=Scale; Sheet=Page 1 de 1
  Height = 215.9
  Orientation = 1
  Width = 279.4
FEATURE [TechDraw::DrawViewPart] View001
  CoarseView = false
  Direction = (0.207,0.686,-0.698)
  Focus = 100
  HardHidden = false
  IsoCount = 0
  IsoHidden = false
  IsoVisible = false
  LockPosition = false
  Perspective = false
  Rotation = 0
  Scale = 0.7
  ScaleType = 0
  SeamHidden = false
  SeamVisible = true
  SmoothHidden = false
  SmoothVisible = true
  Source = -> [Body,Body001,Body010]
  X = 146.884
  XDirection = (-0.176,0.728,0.663)
  XSource = -> [LinkGroup,LinkGroup001]
  Y = 131.376
FEATURE [TechDraw::DrawPage] Page
  KeepUpdated = true
  NextBalloonIndex = 1
  ProjectionType = 0
  Template = -> Template
  Views = -> [View001]
FEATURE [Sketcher::SketchObject] Sketch016
  FullyConstrained = true
  MapMode = 5
  Support = -> [XY_Plane011]
  sketch-geometry (8):
    g0: ArcOfCircle CenterX=0 CenterY=-2.3e-15 CenterZ=0 NormalX=0 NormalY=0 NormalZ=1 AngleXU=0 Radius=23.8 StartAngle=2.2259 EndAngle=4.05728
    g1: ArcOfCircle CenterX=0 CenterY=-2.3e-15 CenterZ=0 NormalX=0 NormalY=0 NormalZ=1 AngleXU=0 Radius=23.8 StartAngle=5.3675 EndAngle=7.19888
    g2: LineSegment StartX=-14.5 StartY=-18.873 StartZ=0 EndX=14.5 EndY=-18.873 EndZ=0
    g3: LineSegment StartX=-14.5 StartY=18.873 StartZ=0 EndX=14.5 EndY=18.873 EndZ=0
    g4: ArcOfCircle CenterX=0 CenterY=-2.3e-15 CenterZ=0 NormalX=0 NormalY=0 NormalZ=1 AngleXU=0 Radius=22.6 StartAngle=2.22941 EndAngle=4.05377
    g5: ArcOfCircle CenterX=0 CenterY=-2.3e-15 CenterZ=0 NormalX=0 NormalY=0 NormalZ=1 AngleXU=0 Radius=22.6 StartAngle=5.371 EndAngle=7.19537
    g6: LineSegment StartX=-13.8317 StartY=17.873 StartZ=0 EndX=13.8317 EndY=17.873 EndZ=0
    g7: LineSegment StartX=13.8317 StartY=-17.873 StartZ=0 EndX=-13.8317 EndY=-17.873 EndZ=0
  constraints (22):
    c: Coincident(g0,g-1)
    c: Coincident(g0,g1)
    c: Coincident(g0,g2)
    c: Coincident(g1,g2)
    c: Coincident(g1,g3)
    c: Coincident(g0,g3)
    c: Symmetric(g1,g0,g-2)
    c: Symmetric(g0,g1,g-2)
    c: Radius(g1) = 23.8
    c: Symmetric(g0,g0,g-1)
    c: DistanceX(g2,g2) = 29
    c: Coincident(g4,g0)
    c: Coincident(g5,g0)
    c: Coincident(g6,g4)
    c: Coincident(g6,g5)
    c: Coincident(g7,g5)
    c: Coincident(g7,g4)
    c: Symmetric(g5,g5,g-1)
    c: Symmetric(g5,g4,g-2)
    c: Radius(g5) = 22.6
    c: Horizontal(g7)
    c: Distance(g4,g3) = 1
FEATURE [PartDesign::Pad] Pad010
  Direction = (1,1,1)
  Length = 10
  Length2 = 100
  Profile = -> Sketch016
  Type = 0
FEATURE [PartDesign::Chamfer] Chamfer003
  Angle = 45
  Base = -> Pad010 [Edge7,Edge12]
  BaseFeature = -> Pad010
  ChamferType = 0
  FlipDirection = false
  Size = 0.5
  Size2 = 1
  SupportTransform = false
FEATURE [Sketcher::SketchObject] Sketch017
  FullyConstrained = true
  MapMode = 5
  Placement = pos=(0,0,0) rot=(1,0,0;3.14159rad)
  Support = -> [Chamfer003]
  sketch-geometry (2):
    g0: Circle CenterX=0 CenterY=0 CenterZ=0 NormalX=0 NormalY=0 NormalZ=1 AngleXU=0 Radius=23.9
    g1: Circle CenterX=0 CenterY=0 CenterZ=0 NormalX=0 NormalY=0 NormalZ=1 AngleXU=0 Radius=22.6
  constraints (4):
    c: Coincident(g0,g-1)
    c: Radius(g0) = 23.9
    c: Coincident(g1,g0)
    c: Radius(g1) = 22.6
FEATURE [PartDesign::Pad] Pad011
  BaseFeature = -> Chamfer003
  Direction = (1,1,1)
  Length = 20
  Length2 = 100
  Profile = -> Sketch017
  Type = 0
FEATURE [Sketcher::SketchObject] Sketch018
  ExternalGeometry = -> [Pad011]
  FullyConstrained = true
  MapMode = 5
  Placement = pos=(0,0,0) rot=(1,0,0;3.14159rad)
  Support = -> [Pad011]
  sketch-geometry (4):
    g0: ArcOfCircle CenterX=-1.1e-15 CenterY=0 CenterZ=0 NormalX=0 NormalY=0 NormalZ=1 AngleXU=0 Radius=23.9 StartAngle=3.98637 EndAngle=5.43841
    g1: ArcOfCircle CenterX=-1.1e-15 CenterY=0 CenterZ=0 NormalX=0 NormalY=0 NormalZ=1 AngleXU=0 Radius=23.9 StartAngle=0.844779 EndAngle=2.29681
    g2: LineSegment StartX=-15.8671 StartY=17.873 StartZ=0 EndX=15.8671 EndY=17.873 EndZ=0
    g3: LineSegment StartX=-15.8671 StartY=-17.873 StartZ=0 EndX=15.8671 EndY=-17.873 EndZ=0
  constraints (14):
    c: Coincident(g0,g-1)
    c: PointOnObject(g0,g-3)
    c: PointOnObject(g0,g-3)
    c: Coincident(g1,g0)
    c: PointOnObject(g1,g-3)
    c: PointOnObject(g1,g-3)
    c: Coincident(g2,g1)
    c: Coincident(g2,g1)
    c: Horizontal(g2)
    c: PointOnObject(g-4,g2)
    c: Coincident(g3,g0)
    c: Coincident(g3,g0)
    c: Horizontal(g3)
    c: PointOnObject(g-5,g3)
FEATURE [PartDesign::Pad] Pad012
  BaseFeature = -> Pad011
  Direction = (1,1,1)
  Length = 2
  Length2 = 100
  Profile = -> Sketch018
  Type = 0
FEATURE [Sketcher::SketchObject] Sketch019
  ExternalGeometry = -> [Pad012]
  FullyConstrained = true
  MapMode = 5
  Placement = pos=(0,0,-20) rot=(1,0,0;3.14159rad)
  Support = -> [Pad012]
  sketch-geometry (3):
    g0: Circle CenterX=-18 CenterY=4 CenterZ=0 NormalX=0 NormalY=0 NormalZ=1 AngleXU=0 Radius=1.5
    g1: Circle CenterX=-18 CenterY=-4 CenterZ=0 NormalX=0 NormalY=0 NormalZ=1 AngleXU=0 Radius=1.5
    g2: Circle CenterX=0 CenterY=0 CenterZ=0 NormalX=0 NormalY=0 NormalZ=1 AngleXU=0 Radius=23.9
  constraints (7):
    c: Radius(g1) = 1.5
    c: Equal(g1,g0)
    c: Symmetric(g0,g1,g-1)
    c: DistanceX(g0) = -18
    c: DistanceY(g0) = 4
    c: Radius(g2) = 23.9
    c: Coincident(g2,g-1)
FEATURE [PartDesign::Pad] Pad013
  BaseFeature = -> Pad012
  Direction = (1,1,1)
  Length = 2
  Length2 = 100
  Profile = -> Sketch019
  Type = 0
FEATURE [PartDesign::Chamfer] Chamfer004
  Angle = 45
  Base = -> Pad013 [Edge42]
  BaseFeature = -> Pad013
  ChamferType = 0
  FlipDirection = false
  Size = 1
  Size2 = 1
  SupportTransform = false
FEATURE [PartDesign::Body] Body011  label="couvercle_coiffe_V1"
  Group = -> [Sketch016,Pad010,Chamfer003,Sketch017,Pad011,Sketch018,Pad012,Sketch019,Pad013,Chamfer004]
  Origin = -> Origin011
  Placement = pos=(0,0,200.3) rot=(0,0,1;0rad)
  Tip = -> Chamfer004
FEATURE [Mesh::Feature] Mesh001  label="couvercle_coiffe_V1 (Meshed)"
FEATURE [Sketcher::SketchObject] Sketch020
  FullyConstrained = true
  MapMode = 5
  Support = -> [XY_Plane012]
  sketch-geometry (2):
    g0: Circle CenterX=0 CenterY=0 CenterZ=0 NormalX=0 NormalY=0 NormalZ=1 AngleXU=0 Radius=9.25
    g1: Circle CenterX=0 CenterY=0 CenterZ=0 NormalX=0 NormalY=0 NormalZ=1 AngleXU=0 Radius=11.75
  constraints (4):
    c: Coincident(g0,g-1)
    c: Coincident(g1,g0)
    c: Radius(g1) = 11.75
    c: Radius(g0) = 9.25
FEATURE [PartDesign::Pad] Pad014
  Direction = (1,1,1)
  Length = 70
  Length2 = 100
  Profile = -> Sketch020
  Type = 0
FEATURE [Sketcher::SketchObject] Sketch021
  FullyConstrained = true
  MapMode = 5
  Placement = pos=(0,0,0) rot=(1,0,0;3.14159rad)
  Support = -> [Pad014]
  sketch-geometry (4):
    g0: LineSegment StartX=-15.74 StartY=1.5 StartZ=0 EndX=15.74 EndY=1.5 EndZ=0
    g1: LineSegment StartX=15.74 StartY=1.5 StartZ=0 EndX=15.74 EndY=-1.5 EndZ=0
    g2: LineSegment StartX=15.74 StartY=-1.5 StartZ=0 EndX=-15.74 EndY=-1.5 EndZ=0
    g3: LineSegment StartX=-15.74 StartY=-1.5 StartZ=0 EndX=-15.74 EndY=1.5 EndZ=0
  constraints (11):
    c: Coincident(g0,g1)
    c: Coincident(g1,g2)
    c: Coincident(g2,g3)
    c: Coincident(g3,g0)
    c: Horizontal(g0)
    c: Horizontal(g2)
    c: Vertical(g1)
    c: Vertical(g3)
    c: Symmetric(g1,g0,g-1)
    c: DistanceX(g2,g2) = 31.48
    c: DistanceY(g1,g1) = 3
FEATURE [PartDesign::Pocket] Pocket004
  BaseFeature = -> Pad014
  Length = 67
  Length2 = 100
  Profile = -> Sketch021
  Type = 0
FEATURE [PartDesign::Chamfer] Chamfer005
  Angle = 45
  Base = -> Pocket004 [Edge3,Edge7]
  BaseFeature = -> Pocket004
  ChamferType = 0
  FlipDirection = false
  Size = 2
  Size2 = 1
  SupportTransform = false
FEATURE [Sketcher::SketchObject] Sketch022
  FullyConstrained = true
  MapMode = 5
  Placement = pos=(0,0,0) rot=(1,0,0;3.14159rad)
  Support = -> [Chamfer005]
  sketch-geometry (4):
    g0: LineSegment StartX=-1.5 StartY=15.795 StartZ=0 EndX=1.5 EndY=15.795 EndZ=0
    g1: LineSegment StartX=1.5 StartY=15.795 StartZ=0 EndX=1.5 EndY=-15.795 EndZ=0
    g2: LineSegment StartX=1.5 StartY=-15.795 StartZ=0 EndX=-1.5 EndY=-15.795 EndZ=0
    g3: LineSegment StartX=-1.5 StartY=-15.795 StartZ=0 EndX=-1.5 EndY=15.795 EndZ=0
  constraints (11):
    c: Coincident(g0,g1)
    c: Coincident(g1,g2)
    c: Coincident(g2,g3)
    c: Coincident(g3,g0)
    c: Horizontal(g0)
    c: Horizontal(g2)
    c: Vertical(g1)
    c: Vertical(g3)
    c: Symmetric(g1,g0,g-1)
    c: DistanceX(g2,g2) = 3
    c: DistanceY(g1,g1) = 31.59
FEATURE [PartDesign::Pocket] Pocket005
  BaseFeature = -> Chamfer005
  Length = 67
  Length2 = 100
  Profile = -> Sketch022
  Type = 0
FEATURE [PartDesign::Body] Body012  label="Adaptateur_moteur_V1"
  Group = -> [Sketch020,Pad014,Sketch021,Pocket004,Chamfer005,Sketch022,Pocket005]
  Origin = -> Origin012
  Placement = pos=(0,8e-15,69) rot=(1,0,0;3.14159rad)
  Tip = -> Pocket005
FEATURE [Mesh::Feature] Mesh002  label="couvercle_coiffe_V1 (Meshed)001"
FEATURE [Sketcher::SketchObject] Sketch023
  FullyConstrained = true
  MapMode = 5
  Support = -> [XY_Plane013]
  sketch-geometry (2):
    g0: Circle CenterX=0 CenterY=0 CenterZ=0 NormalX=0 NormalY=0 NormalZ=1 AngleXU=0 Radius=9.25
    g1: Circle CenterX=0 CenterY=0 CenterZ=0 NormalX=0 NormalY=0 NormalZ=1 AngleXU=0 Radius=11.75
  constraints (4):
    c: Coincident(g0,g-1)
    c: Coincident(g1,g0)
    c: Radius(g1) = 11.75
    c: Radius(g0) = 9.25
FEATURE [PartDesign::Pad] Pad015
  Direction = (1,1,1)
  Length = 70
  Length2 = 100
  Profile = -> Sketch023
  Type = 0
FEATURE [Sketcher::SketchObject] Sketch025
  FullyConstrained = true
  MapMode = 5
  Placement = pos=(0,0,0) rot=(1,0,0;3.14159rad)
  Support = -> [Pad015]
  sketch-geometry (4):
    g0: LineSegment StartX=-15.74 StartY=1.5 StartZ=0 EndX=15.74 EndY=1.5 EndZ=0
    g1: LineSegment StartX=15.74 StartY=1.5 StartZ=0 EndX=15.74 EndY=-1.5 EndZ=0
    g2: LineSegment StartX=15.74 StartY=-1.5 StartZ=0 EndX=-15.74 EndY=-1.5 EndZ=0
    g3: LineSegment StartX=-15.74 StartY=-1.5 StartZ=0 EndX=-15.74 EndY=1.5 EndZ=0
  constraints (11):
    c: Coincident(g0,g1)
    c: Coincident(g1,g2)
    c: Coincident(g2,g3)
    c: Coincident(g3,g0)
    c: Horizontal(g0)
    c: Horizontal(g2)
    c: Vertical(g1)
    c: Vertical(g3)
    c: Symmetric(g1,g0,g-1)
    c: DistanceX(g2,g2) = 31.48
    c: DistanceY(g1,g1) = 3
FEATURE [PartDesign::Pocket] Pocket007
  BaseFeature = -> Pad015
  Length = 67
  Length2 = 100
  Profile = -> Sketch025
  Type = 0
FEATURE [PartDesign::Chamfer] Chamfer006
  Angle = 45
  Base = -> Pocket007 [Edge3,Edge7]
  BaseFeature = -> Pocket007
  ChamferType = 0
  FlipDirection = false
  Size = 2
  Size2 = 1
  SupportTransform = false
FEATURE [Sketcher::SketchObject] Sketch024
  ExternalGeometry = -> [Chamfer006]
  FullyConstrained = true
  MapMode = 5
  Placement = pos=(0,0,0) rot=(1,0,0;3.14159rad)
  Support = -> [Chamfer006]
  sketch-geometry (8):
    g0: LineSegment StartX=-1.5 StartY=13.94 StartZ=0 EndX=11.6539 EndY=13.94 EndZ=0
    g1: LineSegment StartX=11.6539 StartY=13.94 StartZ=0 EndX=11.6539 EndY=1.5 EndZ=0
    g2: LineSegment StartX=11.6539 StartY=1.5 StartZ=0 EndX=-1.5 EndY=1.5 EndZ=0
    g3: LineSegment StartX=-1.5 StartY=1.5 StartZ=0 EndX=-1.5 EndY=13.94 EndZ=0
    g4: LineSegment StartX=-11.6539 StartY=-1.5 StartZ=0 EndX=1.5 EndY=-1.5 EndZ=0
    g5: LineSegment StartX=1.5 StartY=-1.5 StartZ=0 EndX=1.5 EndY=-13.94 EndZ=0
    g6: LineSegment StartX=1.5 StartY=-13.94 StartZ=0 EndX=-11.6539 EndY=-13.94 EndZ=0
    g7: LineSegment StartX=-11.6539 StartY=-13.94 StartZ=0 EndX=-11.6539 EndY=-1.5 EndZ=0
  constraints (21):
    c: Coincident(g0,g1)
    c: Coincident(g1,g2)
    c: Coincident(g2,g3)
    c: Coincident(g3,g0)
    c: Horizontal(g0)
    c: Horizontal(g2)
    c: Vertical(g1)
    c: Vertical(g3)
    c: Coincident(g1,g-3)
    c: DistanceX(g-2,g0) = -1.5
    c: DistanceY(g1,g1) = 12.44
    c: Coincident(g4,g5)
    c: Coincident(g5,g6)
    c: Coincident(g6,g7)
    c: Coincident(g7,g4)
    c: Horizontal(g4)
    c: Horizontal(g6)
    c: Vertical(g5)
    c: Vertical(g7)
    c: Coincident(g4,g-4)
    c: Symmetric(g5,g0,g-1)
FEATURE [PartDesign::Pocket] Pocket006
  BaseFeature = -> Chamfer006
  Length = 67
  Length2 = 100
  Profile = -> Sketch024
  Type = 0
FEATURE [PartDesign::Body] Body013  label="Adaptateur_moteur_V2"
  Group = -> [Sketch023,Pad015,Sketch025,Pocket007,Chamfer006,Sketch024,Pocket006]
  Origin = -> Origin013
  Placement = pos=(0,8e-15,69) rot=(1,0,0;3.14159rad)
  Tip = -> Pocket006
FEATURE [Sketcher::SketchObject] Sketch026
  FullyConstrained = true
  MapMode = 5
  Placement = pos=(0,0,0) rot=(0.57735,0.57735,0.57735;2.0944rad)
  Support = -> [YZ_Plane014]
  sketch-geometry (4):
    g0: LineSegment StartX=12.5 StartY=0 StartZ=0 EndX=-12.5 EndY=0 EndZ=0
    g1: LineSegment StartX=-12.5 StartY=0 StartZ=0 EndX=-12.5 EndY=80 EndZ=0
    g2: LineSegment StartX=-12.5 StartY=80 StartZ=0 EndX=12.5 EndY=80 EndZ=0
    g3: LineSegment StartX=12.5 StartY=80 StartZ=0 EndX=12.5 EndY=0 EndZ=0
  constraints (11):
    c: Coincident(g0,g1)
    c: Coincident(g1,g2)
    c: Coincident(g2,g3)
    c: Coincident(g3,g0)
    c: Horizontal(g0)
    c: Vertical(g1)
    c: Vertical(g3)
    c: PointOnObject(g0,g-1)
    c: Symmetric(g1,g2,g-2)
    c: DistanceX(g2,g2) = 25
    c: DistanceY(g3,g3) = 80
FEATURE [PartDesign::Pad] Pad016
  Direction = (1,1,1)
  Length = 27
  Length2 = 100
  Midplane = true
  Placement = pos=(0,0,0) rot=(0.57735,0.57735,0.57735;2.0944rad)
  Profile = -> Sketch026
  Type = 0
FEATURE [PartDesign::Body] Body014  label="Charge_utile_V1"
  Group = -> [Sketch026,Pad016]
  Origin = -> Origin014
  Placement = pos=(0,0,201) rot=(0,0,1;0rad)
  Tip = -> Pad016
FEATURE [Sketcher::SketchObject] Sketch027
  FullyConstrained = true
  MapMode = 5
  Support = -> [XY_Plane015]
  sketch-geometry (12):
    g0: LineSegment StartX=0 StartY=0 StartZ=0 EndX=134.73 EndY=0 EndZ=0
    g1: LineSegment StartX=134.73 StartY=-24 StartZ=0 EndX=134.73 EndY=0 EndZ=0
    g2: LineSegment StartX=134.73 StartY=-24 StartZ=0 EndX=120.272 EndY=-24 EndZ=0
    g3-g7: Circle x5 (B-spline internal-alignment scaffolding for g8; pole/knot coordinates omitted)
    g8: BSplineCurve PolesCount=5 KnotsCount=3 Degree=3 IsPeriodic=0
    g9: GeomPoint X=120.272 Y=-24 Z=0
    g10: GeomPoint X=62.1183 Y=-19.6849 Z=0
    g11: GeomPoint X=0 Y=0 Z=0
  constraints (23):
    c: Coincident(g0,g-1)
    c: PointOnObject(g0,g-1)
    c: Coincident(g1,g0)
    c: Vertical(g1)
    c: Coincident(g2,g1)
    c: Horizontal(g2)
    c: Coincident(g8,g2)
    c: Weight(g3) = 1
    c: Equal(g3, g4-g7) x4
    c: Coincident(g8,g0)
    c: InternalAlignment(g3-g7 -> g8) x5
    c: InternalAlignment(g9,g8)
    c: InternalAlignment(g10,g8)
    c: InternalAlignment(g11,g8)
    c: DistanceX(g6) = 33.4091
    c: DistanceY(g6) = -14.1378
    c: DistanceX(g5) = 61.0359
    c: DistanceY(g5) = -20.426
    c: DistanceX(g4) = 92.9923
    c: DistanceY(g4) = -23.75
    c: DistanceX(g2) = 120.272
    c: DistanceY(g2) = -24
    c: DistanceX(g0,g0) = 134.73
FEATURE [PartDesign::Revolution] Revolution002
  Angle = 360
  Axis = (1,0,0)
  Base = (0,0,0)
  Profile = -> Sketch027
  ReferenceAxis = -> X_Axis015
  Reversed = true
FEATURE [PartDesign::Thickness] Thickness001
  Base = -> Revolution002 [Face1]
  BaseFeature = -> Revolution002
  Intersection = false
  Join = 0
  Mode = 0
  SupportTransform = false
  Value = 1
FEATURE [Sketcher::SketchObject] Sketch028
  FullyConstrained = true
  MapMode = 5
  Placement = pos=(134.73,0,0) rot=(0.57735,0.57735,0.57735;2.0944rad)
  Support = -> [Thickness001]
  sketch-geometry (5):
    g0: Circle CenterX=1.1e-15 CenterY=0 CenterZ=0 NormalX=0 NormalY=0 NormalZ=1 AngleXU=0 Radius=25
    g1: ArcOfCircle CenterX=1.1e-15 CenterY=0 CenterZ=0 NormalX=0 NormalY=0 NormalZ=1 AngleXU=0 Radius=24 StartAngle=0.675132 EndAngle=2.46646
    g2: ArcOfCircle CenterX=1.1e-15 CenterY=0 CenterZ=0 NormalX=0 NormalY=0 NormalZ=1 AngleXU=0 Radius=24 StartAngle=3.81672 EndAngle=5.60805
    g3: LineSegment StartX=-18.735 StartY=15 StartZ=0 EndX=-18.735 EndY=-15 EndZ=0
    g4: LineSegment StartX=18.735 StartY=15 StartZ=0 EndX=18.735 EndY=-15 EndZ=0
  constraints (14):
    c: Coincident(g0,g-1)
    c: Radius(g0) = 25
    c: Coincident(g1,g0)
    c: Coincident(g2,g0)
    c: Symmetric(g2,g2,g-2)
    c: Symmetric(g2,g1,g-1)
    c: Radius(g1) = 24
    c: Equal(g1,g2)
    c: Coincident(g3,g1)
    c: Coincident(g3,g2)
    c: Coincident(g4,g1)
    c: Coincident(g4,g2)
    c: Symmetric(g1,g1,g-2)
    c: DistanceY(g4,g4) = 30
FEATURE [PartDesign::Pad] Pad017
  BaseFeature = -> Thickness001
  Direction = (1,1,1)
  Length = 10
  Length2 = 100
  Profile = -> Sketch028
  Reversed = true
  Type = 0
FEATURE [PartDesign::Chamfer] Chamfer007
  Angle = 45
  Base = -> Pad017 [Edge9,Edge6]
  BaseFeature = -> Pad017
  ChamferType = 0
  FlipDirection = false
  Size = 1
  Size2 = 1
  SupportTransform = false
FEATURE [Sketcher::SketchObject] Sketch029
  FullyConstrained = true
  MapMode = 5
  Support = -> [XY_Plane016]
  sketch-geometry (8):
    g0: ArcOfCircle CenterX=0 CenterY=-2.3e-15 CenterZ=0 NormalX=0 NormalY=0 NormalZ=1 AngleXU=0 Radius=23.8 StartAngle=2.2259 EndAngle=4.05728
    g1: ArcOfCircle CenterX=0 CenterY=-2.3e-15 CenterZ=0 NormalX=0 NormalY=0 NormalZ=1 AngleXU=0 Radius=23.8 StartAngle=5.3675 EndAngle=7.19888
    g2: LineSegment StartX=-14.5 StartY=-18.873 StartZ=0 EndX=14.5 EndY=-18.873 EndZ=0
    g3: LineSegment StartX=-14.5 StartY=18.873 StartZ=0 EndX=14.5 EndY=18.873 EndZ=0
    g4: ArcOfCircle CenterX=0 CenterY=-2.3e-15 CenterZ=0 NormalX=0 NormalY=0 NormalZ=1 AngleXU=0 Radius=22.6 StartAngle=2.22941 EndAngle=4.05377
    g5: ArcOfCircle CenterX=0 CenterY=-2.3e-15 CenterZ=0 NormalX=0 NormalY=0 NormalZ=1 AngleXU=0 Radius=22.6 StartAngle=5.371 EndAngle=7.19537
    g6: LineSegment StartX=-13.8317 StartY=17.873 StartZ=0 EndX=13.8317 EndY=17.873 EndZ=0
    g7: LineSegment StartX=13.8317 StartY=-17.873 StartZ=0 EndX=-13.8317 EndY=-17.873 EndZ=0
  constraints (22):
    c: Coincident(g0,g-1)
    c: Coincident(g0,g1)
    c: Coincident(g0,g2)
    c: Coincident(g1,g2)
    c: Coincident(g1,g3)
    c: Coincident(g0,g3)
    c: Symmetric(g1,g0,g-2)
    c: Symmetric(g0,g1,g-2)
    c: Radius(g1) = 23.8
    c: Symmetric(g0,g0,g-1)
    c: DistanceX(g2,g2) = 29
    c: Coincident(g4,g0)
    c: Coincident(g5,g0)
    c: Coincident(g6,g4)
    c: Coincident(g6,g5)
    c: Coincident(g7,g5)
    c: Coincident(g7,g4)
    c: Symmetric(g5,g5,g-1)
    c: Symmetric(g5,g4,g-2)
    c: Radius(g5) = 22.6
    c: Horizontal(g7)
    c: Distance(g4,g3) = 1
FEATURE [PartDesign::Pad] Pad018
  Direction = (1,1,1)
  Length = 10
  Length2 = 100
  Profile = -> Sketch029
  Type = 0
FEATURE [PartDesign::Chamfer] Chamfer008
  Angle = 45
  Base = -> Pad018 [Edge7,Edge12]
  BaseFeature = -> Pad018
  ChamferType = 0
  FlipDirection = false
  Size = 0.5
  Size2 = 1
  SupportTransform = false
FEATURE [Sketcher::SketchObject] Sketch030
  FullyConstrained = true
  MapMode = 5
  Placement = pos=(0,0,0) rot=(1,0,0;3.14159rad)
  Support = -> [Chamfer008]
  sketch-geometry (2):
    g0: Circle CenterX=0 CenterY=0 CenterZ=0 NormalX=0 NormalY=0 NormalZ=1 AngleXU=0 Radius=23.9
    g1: Circle CenterX=0 CenterY=0 CenterZ=0 NormalX=0 NormalY=0 NormalZ=1 AngleXU=0 Radius=22.6
  constraints (4):
    c: Coincident(g0,g-1)
    c: Radius(g0) = 23.9
    c: Coincident(g1,g0)
    c: Radius(g1) = 22.6
FEATURE [PartDesign::Pad] Pad019
  BaseFeature = -> Chamfer008
  Direction = (1,1,1)
  Length = 12
  Length2 = 100
  Profile = -> Sketch030
  Type = 0
FEATURE [Sketcher::SketchObject] Sketch031
  ExternalGeometry = -> [Pad019]
  FullyConstrained = true
  MapMode = 5
  Placement = pos=(0,0,0) rot=(1,0,0;3.14159rad)
  Support = -> [Pad019]
  sketch-geometry (4):
    g0: ArcOfCircle CenterX=-1.1e-15 CenterY=0 CenterZ=0 NormalX=0 NormalY=0 NormalZ=1 AngleXU=0 Radius=23.9 StartAngle=3.98637 EndAngle=5.43841
    g1: ArcOfCircle CenterX=-1.1e-15 CenterY=0 CenterZ=0 NormalX=0 NormalY=0 NormalZ=1 AngleXU=0 Radius=23.9 StartAngle=0.844779 EndAngle=2.29681
    g2: LineSegment StartX=-15.8671 StartY=17.873 StartZ=0 EndX=15.8671 EndY=17.873 EndZ=0
    g3: LineSegment StartX=-15.8671 StartY=-17.873 StartZ=0 EndX=15.8671 EndY=-17.873 EndZ=0
  constraints (14):
    c: Coincident(g0,g-1)
    c: PointOnObject(g0,g-3)
    c: PointOnObject(g0,g-3)
    c: Coincident(g1,g0)
    c: PointOnObject(g1,g-3)
    c: PointOnObject(g1,g-3)
    c: Coincident(g2,g1)
    c: Coincident(g2,g1)
    c: Horizontal(g2)
    c: PointOnObject(g-4,g2)
    c: Coincident(g3,g0)
    c: Coincident(g3,g0)
    c: Horizontal(g3)
    c: PointOnObject(g-5,g3)
FEATURE [PartDesign::Pad] Pad020
  BaseFeature = -> Pad019
  Direction = (1,1,1)
  Length = 2
  Length2 = 100
  Profile = -> Sketch031
  Type = 0
FEATURE [Sketcher::SketchObject] Sketch032
  ExternalGeometry = -> [Pad020]
  FullyConstrained = true
  MapMode = 5
  Placement = pos=(0,0,-12) rot=(1,0,0;3.14159rad)
  Support = -> [Pad020]
  sketch-geometry (3):
    g0: Circle CenterX=0 CenterY=0 CenterZ=0 NormalX=0 NormalY=0 NormalZ=1 AngleXU=0 Radius=23.9
    g1: Circle CenterX=-18 CenterY=3.5 CenterZ=0 NormalX=0 NormalY=0 NormalZ=1 AngleXU=0 Radius=1.5
    g2: Circle CenterX=-18 CenterY=-3.5 CenterZ=0 NormalX=0 NormalY=0 NormalZ=1 AngleXU=0 Radius=1.5
  constraints (8):
    c: Coincident(g0,g-1)
    c: Radius(g-3) = 23.9
    c: Radius(g0) = 23.9
    c: Radius(g2) = 1.5
    c: Equal(g2,g1)
    c: Symmetric(g1,g2,g-1)
    c: DistanceX(g-2,g1) = -18
    c: DistanceY(g-1,g1) = 3.5
FEATURE [PartDesign::Pad] Pad021
  BaseFeature = -> Pad020
  Direction = (1,1,1)
  Length = 2
  Length2 = 100
  Profile = -> Sketch032
  Type = 0
FEATURE [PartDesign::Body] Body016  label="couvercle_coiffe_V002"
  Group = -> [Sketch029,Pad018,Chamfer008,Sketch030,Pad019,Sketch031,Pad020,Sketch032,Pad021]
  Origin = -> Origin016
  Placement = pos=(0,0,200.3) rot=(0,0,1;0rad)
  Tip = -> Pad021
FEATURE [Sketcher::SketchObject] Sketch033
  FullyConstrained = true
  MapMode = 5
  Placement = pos=(0,0,0) rot=(1,0,0;1.5708rad)
  Support = -> [XZ_Plane015]
  sketch-geometry (4):
    g0: LineSegment StartX=-0.5 StartY=0 StartZ=0 EndX=14.5 EndY=0 EndZ=0
    g1: LineSegment StartX=24.4481 StartY=10.14 StartZ=0 EndX=-0.5 EndY=0 EndZ=0
    g2: LineSegment StartX=24.4481 StartY=10.14 StartZ=0 EndX=34.6427 EndY=13.7353 EndZ=0
    g3: LineSegment StartX=34.6427 StartY=13.7353 StartZ=0 EndX=14.5 EndY=0 EndZ=0
  constraints (12):
    c: PointOnObject(g0,g-1)
    c: PointOnObject(g0,g-1)
    c: DistanceX(g0,g0) = 15
    c: DistanceX(g-2,g0) = -0.5
    c: Coincident(g1,g0)
    c: DistanceY(g0,g1) = 10.14
    c: Coincident(g1,g2)
    c: Coincident(g2,g3)
    c: Coincident(g3,g0)
    c: Distance(g3) = 24.38
    c: Distance(g2) = 10.81
    c: Distance(g1) = 26.93
FEATURE [PartDesign::Revolution] Revolution003
  Angle = 360
  Axis = (1,0,0)
  Base = (0,0,0)
  BaseFeature = -> Chamfer007
  Profile = -> Sketch033
  ReferenceAxis = -> Sketch033 [H_Axis]
FEATURE [PartDesign::Body] Body015  label="coiffe_V002"
  Group = -> [Sketch027,Revolution002,Thickness001,Sketch028,Pad017,Chamfer007,Sketch033,Revolution003]
  Origin = -> Origin015
  Placement = pos=(-7.4e-14,0,335) rot=(0,1,0;1.5708rad)
  Tip = -> Revolution003
FEATURE [Mesh::Feature] Mesh003  label="coiffe_V002 (Meshed)"
FEATURE [Mesh::Feature] Mesh004  label="couvercle_coiffe_V002 (Meshed)"
